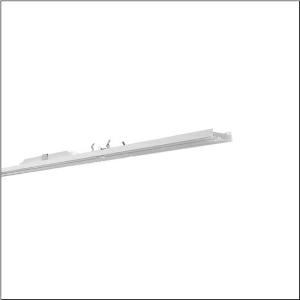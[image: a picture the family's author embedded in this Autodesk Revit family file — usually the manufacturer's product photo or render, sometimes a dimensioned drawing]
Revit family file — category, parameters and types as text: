
# Revit family: licross_r__11_recessed_mo_51ul1edv4e5f_fa7a
name_source: partatom
category: Lighting Fixtures
units: mm (PartAtom-declared; Revit-internal decimal feet)

## family parameters
Cut with Voids When Loaded = No
Host = Face
Light Source = No
Part Type = Normal
Room Calculation Point = No
Round Connector Dimension = Use Diameter
Shared = No

## types (1)
- --- (1 x LED, 14910 lm, 89.6 W, 4000K)
    Apparent Load = 90 VA
    CIE Flux Codes = 85 95 99 100 100
    Color Rendering = 80
    Color Temperature = 4000K
    Default Elevation = 1800 mm
    Description = Licross® 11 Recessed MO, luminaire insert, of sheet steel, galvanised, coil coated, white, length: 2.250mm, width: 66mm, height: 67mm, LED rated luminous flux: 14.910lm, light colour: 840, control gear: DALI 2, control gear: ECG DALI, with terminal, 5-pole, max. 2.5mm², mains connection: 230V, AC, 50/60Hz, rated input power: 90W, halogen-free wiring, primary optical cover: cover, of PMMA, light emission: direct distribution, primary light characteristic: symmetric, protection rating (complete): IP40, insulation class (complete): insulation class I (protective earthing), certification: CE, ENEC, VDE, UKCA, protection symbol: D if used in an environment without relevant dust loads with corresponding accessories, impact resistance: IK06, permissible ambient temperature for indoor applications: -25..+35°C, corresponds to IFS (International Featured Standards) requirements for safety and quality in the food industry, reducing of maximum allowable ambient temperature of 5°C with ceiling mounting, LABS conformity tested according to VDMA 24364:2018-05, packaging unit: 1 piece
    Height = 58 mm
    Lamp = 1 x LED
    Lamp Light Flux = 14910 lm
    Lamp Power = 89.6 W
    Lamp count = 1
    Length = 2250 mm
    Luminous efficacy = 166 lm/W
    Manufacturer = Siteco
    ModVariant = No
    Model = 51UL1EDV4E5F
    Mounting Place = Ceiling
    Mounting Type = Pendant
    Number of Poles = 1
    OnlyDefault = Yes
    Power Factor = 1
    Product Name = Licross® 11 Recessed MO
    Product group = luminaire insert
    ProductGroupID = 901
    Protection Class = Protection class I
    Protection Degree = IP 40
    RLX_Detail_Level = 1
    RLX_Emergency_Light_Flux = 0 lm
    RLX_Emergency_Type = 0
    RLX_Emergency_Type_DB = No
    RlxData = <blob elided: 26849 chars, md5=05e79224>
    Socket = socket
    Standby Power = 0 W
    System Light Flux = 14910 lm
    System Power = 90 W
    Type Comments = factory setting: luminous flux: 100 % | dim-lin: 254 | 400 mA
    Type Image = l_1006953.jpg
    URL = http://relux.com
    VarID = @adj_130637
    Voltage = 0 V
    Weight = 0.00 kg
    Width = 66 mm

## geometry (parser evidence)
native form markers: Blend x4, Sweep x10
no freeform markers — native parametric forms only
